# Revit family: Hager-Orion_Plus-IP66-D200-Cl.II-Poly_encl-630A-ES-es
name_source: partatom
category: Electrical Equipment
units: mm (PartAtom-declared; Revit-internal decimal feet)

## family parameters
Cut with Voids When Loaded = No
Host = Face
Panel Configuration = Two Columns, Circuits Across
Part Type = Panelboard
Room Calculation Point = No
Round Connector Dimension = Use Diameter
Shared = No

## types (3) — shared parameters
EF000003 - Tipo de montaje = EV000384 - Montado superficial (escayola)
EF000007 - Color = EV000270 - Gris
EF000049 - Profundidad = 200 mm  [stored 0.656168 ft]
EF000116 - Número RAL = 7035
EF000118 - Con placa de montaje = No
EF000339 - Tipo de cubierta = EV004216 - Puerta
EF001088 - Posibilidad de extensión = No
EF001131 - Profundidad interna = 200 mm  [stored 0.656168 ft]
EF001596 - Material de la carcasa = EV000139 - Plástico
EF003532 - Adecuado para uso en exteriores = Yes
EF004293 - Resistencia al impacto (IK) = EV008784 - IK10
EF004464 - Tipo de puerta = EV002646 - Único
EF005474 - Grado de protección (IP) = EV006422 - IP66
EF006244 - Tapa/puerta transparente = No
EF006306 - Con cierre = Yes
EF007800 - Adecuado para la protección contra rayos = No
EF008873 - Corriente nominal (In) = 630 A
EF009170 - Espesor del material de la caja = 2 mm  [stored 0.00656168 ft]
EF009171 - Espesor puerta/tapa = 2 mm  [stored 0.00656168 ft]
EF009212 - Versión de la cubierta = EV000116 - Cerrado
EF015940 - Tapa con alivio de sobrepresión = No
HG000002 - Con puerta o tapa = Yes
HG000003 - Gama = Orion Plus
HG000006 - Empotrado = No
HG000009 - Puerta batiente doble = No
HG000010 - Puertas asimétricas = No
HG000023 - Caja de doble sección = No
HG000024 - Altura de la sección inferior = 800 mm
HG000026 - Instalación en suelo = No
Manufacturer = Hager
Type Comments = Orion Plus
zero-valued in all types: Default Elevation, EF000218 - Profundidad de instalación, EF000437 - Número de entradas de conductos de cables, EF009554 - Número de aberturas para placas-brida, HG000027 - Altura de zócalo

## per-type parameters (varying)
| type | EF000008 - Anchura | EF000040 - Altura | EF000266 - Número de filas | EF002950 - Anchura de unidades de división | EF004427 - Número de módulos | HG000004 - Referencia del fabricante |
| Montado superficial (escayola) IP66 A300 A500 P200  - FL209B | 300 mm  [stored 0.984252 ft] | 500 mm  [stored 1.64042 ft] | 3 | 12 | 36 | FL209B |
| Montado superficial (escayola) IP66 A400 A500 P200  - FL213B | 400 mm  [stored 1.31234 ft] | 500 mm  [stored 1.64042 ft] | 3 | 18 | 54 | FL213B |
| Montado superficial (escayola) IP66 A400 A650 P200  - FL216B | 400 mm  [stored 1.31234 ft] | 650 mm  [stored 2.13255 ft] | 4 | 18 | 72 | FL216B |

note: [stored X ft] marks values corroborated as IEEE doubles in the binary element streams (Revit-internal decimal feet)

## geometry (parser evidence)
native form markers: Sweep x10
no freeform markers — native parametric forms only
